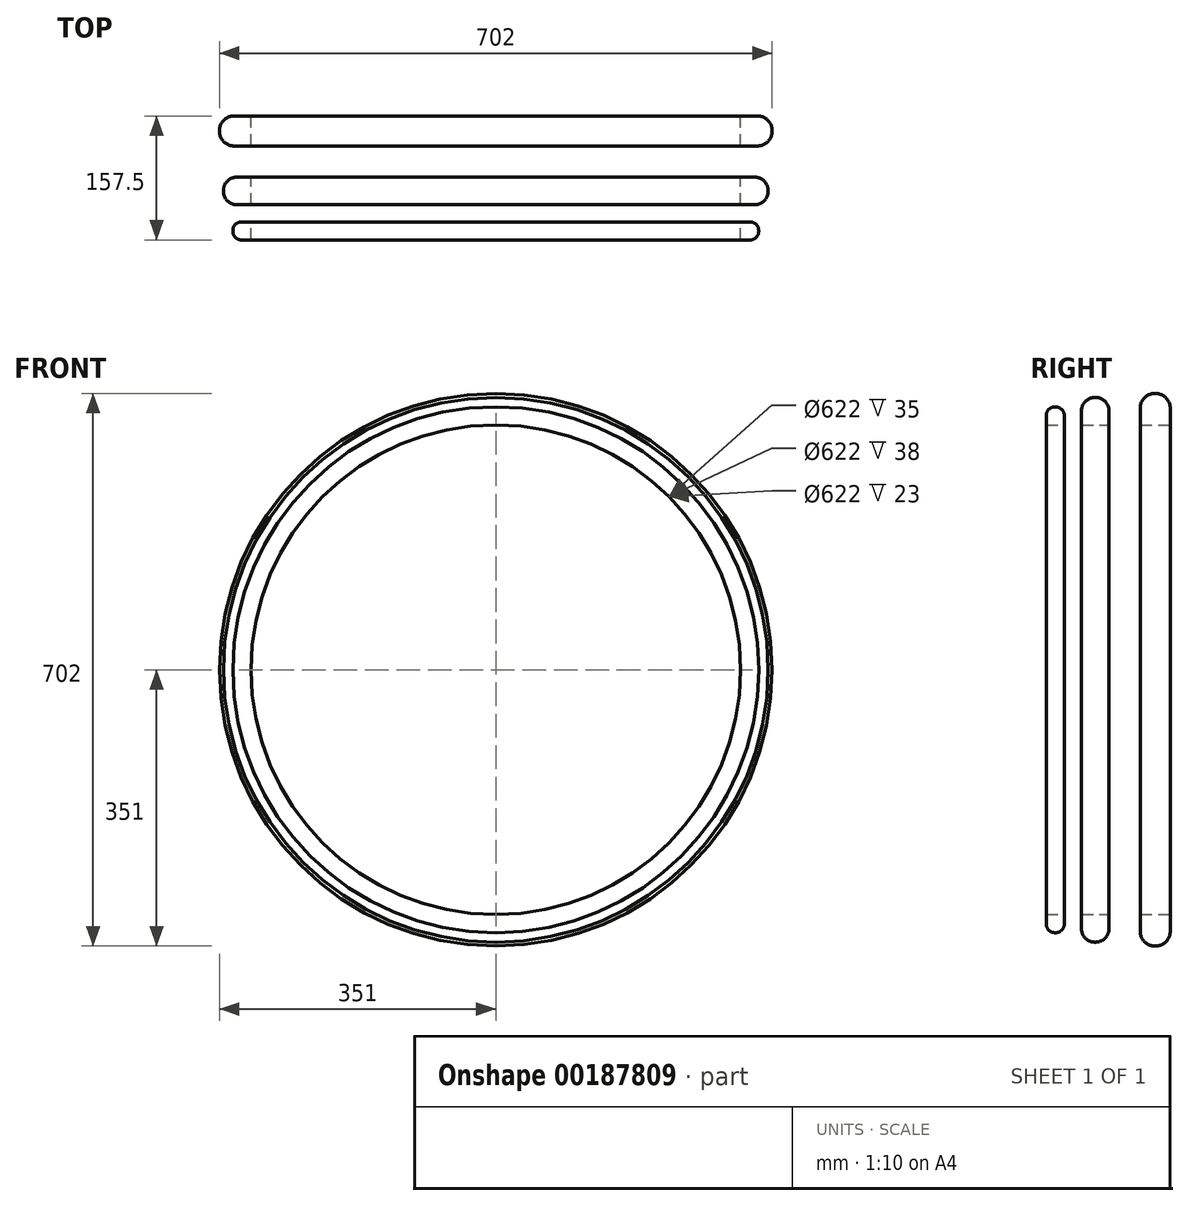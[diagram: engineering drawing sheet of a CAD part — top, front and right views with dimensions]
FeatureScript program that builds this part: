
annotation { "Feature Type Name" : "Feature", "Feature Type Description" : "" }
export const myFeature = defineFeature(function(context is Context, id is Id, definition is map)
    precondition{}
    {
        {
            var Q0;
            Q0=qCreatedBy(makeId("Front.planeOp"),FACE);
            var sketch = newSketch(context, id + "F0", { "sketchPlane" : qUnion([Q0])});
            skCircle(sketch, "E0", {"center": v(0, 0) * mm, "radius": 334 * mm});
            skCircle(sketch, "E1.0", {"center": v(0, 0) * mm, "radius": 311 * mm});
            skSolve(sketch);
        }
        {
            var Q0;
            Q0 = qSketchRegion(id + "F0", true);
            extrude(context, id + "F1", {"entities" : qUnion([Q0]), "endBound" : BoundingType.SYMMETRIC, "depth" : 23 * mm});
        }
        {
            var Q0;
            Q0=makeQuery(id+"F1.opExtrude","CAP_EDGE",EDGE,{"disambiguationData":[OSD([sQuery(id+"F0.wireOp",EDGE,"E0")])],"isStart":false});
            var Q1;
            Q1=makeQuery(id+"F1.opExtrude","CAP_EDGE",EDGE,{"disambiguationData":[OSD([sQuery(id+"F0.wireOp",EDGE,"E0")])],"isStart":true});
            fillet(context, id + "F2", {"entities" : qUnion([Q0, Q1]), "radius" : 11 * mm, "tangentPropagation" : true, "allowEdgeOverflow" : false});
        }
        {
            var Q0;
            Q0=qCreatedBy(makeId("Front.planeOp"),FACE);
            cPlane(context, id + "F3", {"entities" : qUnion([Q0]), "cplaneType" : CPlaneType.OFFSET, "offset" : 50.8 * mm, "oppositeDirection" : true, "width" : 152.4 * mm, "height" : 152.4 * mm});
        }
        {
            var Q0;
            Q0=qCreatedBy(id+"F3.planeOp",FACE);
            var sketch = newSketch(context, id + "F4", { "sketchPlane" : qUnion([Q0])});
            skCircle(sketch, "E2", {"center": v(0, 0) * mm, "radius": 346 * mm});
            skCircle(sketch, "E3.0", {"center": v(0, 0) * mm, "radius": 311 * mm});
            skSolve(sketch);
        }
        {
            var Q0;
            Q0=makeQuery(id+"F4.imprint","IMPRINT",FACE,{"disambiguationData":[TD([[makeQuery(id+"F4.imprint","IMPRINT",EDGE,{"derivedFrom":sQuery(id+"F4.wireOp",EDGE,"E2")}),1.0]])]});
            extrude(context, id + "F5", {"entities" : qUnion([Q0]), "endBound" : BoundingType.SYMMETRIC, "depth" : 35 * mm});
        }
        {
            var Q0;
            Q0=makeQuery(id+"F5.opExtrude","CAP_EDGE",EDGE,{"disambiguationData":[OSD([sQuery(id+"F4.wireOp",EDGE,"E2")])],"isStart":false});
            var Q1;
            Q1=makeQuery(id+"F5.opExtrude","CAP_EDGE",EDGE,{"disambiguationData":[OSD([sQuery(id+"F4.wireOp",EDGE,"E2")])],"isStart":true});
            fillet(context, id + "F6", {"entities" : qUnion([Q0, Q1]), "radius" : 17 * mm, "tangentPropagation" : true, "allowEdgeOverflow" : false});
        }
        {
            var Q0;
            Q0=qCreatedBy(makeId("Front.planeOp"),FACE);
            cPlane(context, id + "F7", {"entities" : qUnion([Q0]), "cplaneType" : CPlaneType.OFFSET, "offset" : 127 * mm, "oppositeDirection" : true, "width" : 152.4 * mm, "height" : 152.4 * mm});
        }
        {
            var Q0;
            Q0=qCreatedBy(id+"F7.planeOp",FACE);
            var sketch = newSketch(context, id + "F8", { "sketchPlane" : qUnion([Q0])});
            skCircle(sketch, "E4", {"center": v(0, 0) * mm, "radius": 351 * mm});
            skCircle(sketch, "E5.0", {"center": v(0, 0) * mm, "radius": 311 * mm});
            skSolve(sketch);
        }
        {
            var Q0;
            Q0=makeQuery(id+"F8.imprint","IMPRINT",FACE,{"disambiguationData":[TD([[makeQuery(id+"F8.imprint","IMPRINT",EDGE,{"derivedFrom":sQuery(id+"F8.wireOp",EDGE,"E4")}),1.0]])]});
            extrude(context, id + "F9", {"entities" : qUnion([Q0]), "endBound" : BoundingType.SYMMETRIC, "depth" : 38 * mm});
        }
        {
            var Q0;
            Q0=makeQuery(id+"F9.opExtrude","CAP_EDGE",EDGE,{"disambiguationData":[OSD([sQuery(id+"F8.wireOp",EDGE,"E4")])],"isStart":false});
            var Q1;
            Q1=makeQuery(id+"F9.opExtrude","CAP_EDGE",EDGE,{"disambiguationData":[OSD([sQuery(id+"F8.wireOp",EDGE,"E4")])],"isStart":true});
            fillet(context, id + "F10", {"entities" : qUnion([Q0, Q1]), "radius" : 18.5 * mm, "tangentPropagation" : true, "allowEdgeOverflow" : false});
        }
    });
